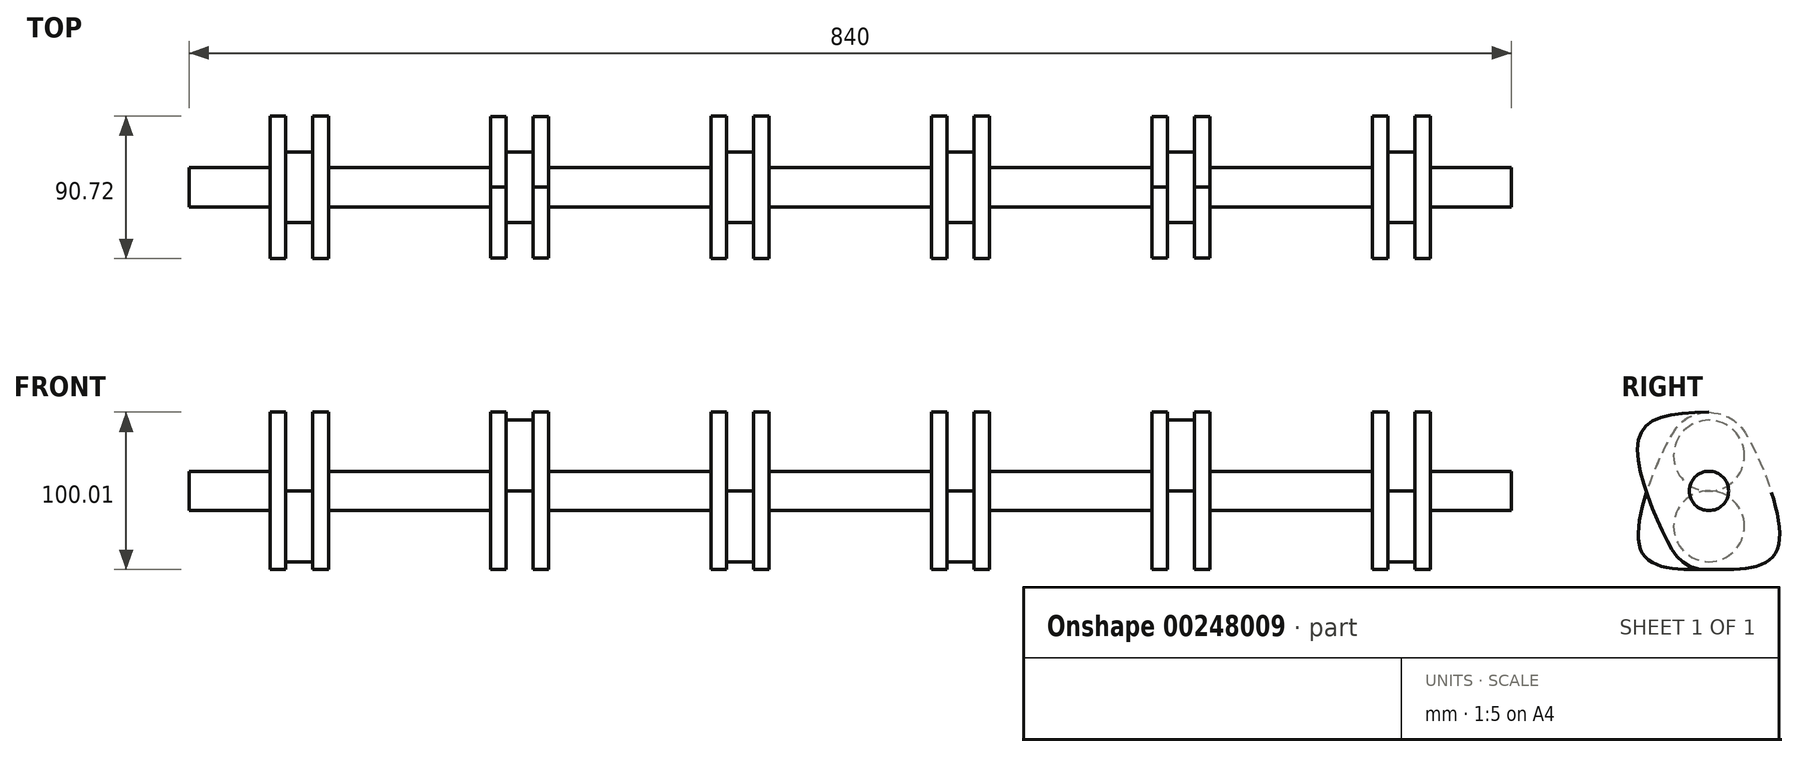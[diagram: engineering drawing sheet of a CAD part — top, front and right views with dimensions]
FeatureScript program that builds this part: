
annotation { "Feature Type Name" : "Feature", "Feature Type Description" : "" }
export const myFeature = defineFeature(function(context is Context, id is Id, definition is map)
    precondition{}
    {
        {
            var Q0;
            Q0=qCreatedBy(makeId("Front.planeOp"),FACE);
            var sketch = newSketch(context, id + "F0", { "sketchPlane" : qUnion([Q0])});
            skLineSegment(sketch, "E0", {"start": v(-435, 99.47) * mm, "end": v(-435, -63.15) * mm, "construction": true});
            skLineSegment(sketch, "E1", {"start": v(435, 93.37) * mm, "end": v(435, -121.08) * mm, "construction": true});
            skSolve(sketch);
        }
        {
            var Q0;
            Q0=qCreatedBy(makeId("Right.planeOp"),FACE);
            cPlane(context, id + "F1", {"entities" : qUnion([Q0]), "cplaneType" : CPlaneType.OFFSET, "offset" : 435 * mm, "width" : 150 * mm, "height" : 150 * mm});
        }
        {
            var Q0;
            Q0=qCreatedBy(id+"F1.planeOp",FACE);
            var sketch = newSketch(context, id + "F2", { "sketchPlane" : qUnion([Q0])});
            skCircle(sketch, "E2", {"center": v(0, 0) * mm, "radius": 12.5 * mm});
            skSolve(sketch);
        }
        {
            var Q0;
            Q0 = qSketchRegion(id + "F2", true);
            extrude(context, id + "F3", {"entities" : qUnion([Q0]), "oppositeDirection" : true, "depth" : 51.5 * mm});
        }
        {
            var Q0;
            Q0=makeQuery(id+"F3.opExtrude","CAP_FACE",FACE,{"disambiguationData":[OSD([sQuery(id+"F2.wireOp",EDGE,"E2")])],"isStart":false});
            var sketch = newSketch(context, id + "F4", { "sketchPlane" : qUnion([Q0])});
            skCircle(sketch, "E3", {"center": v(0, 0) * mm, "radius": 22.5 * mm, "construction": true});
            skLineSegment(sketch, "E4", {"start": v(-49.42, 50) * mm, "end": v(46.28, 50) * mm, "construction": true});
            skLineSegment(sketch, "E5", {"start": v(-54.63, -50) * mm, "end": v(61.91, -50) * mm, "construction": true});
            skFitSpline(sketch, "E6", {"points": [v(0, 50) * mm, v(-44.16, 34.7) * mm, v(-28.23, -28.04) * mm, v(0, -50) * mm], "startDerivative": vector(-213.04, 0) * mm, "endDerivative": vector(172.02, 0) * mm});
            skFitSpline(sketch, "E7.MirrorCS", {"points": [v(0, 50) * mm, v(44.16, 34.7) * mm, v(28.23, -28.04) * mm, v(0, -50) * mm], "startDerivative": vector(213.04, 0) * mm, "endDerivative": vector(-172.02, 0) * mm});
            skFitSpline(sketch, "E8.MirrorCS", {"points": [v(0, 50) * mm, v(44.16, 34.7) * mm, v(28.23, -28.04) * mm, v(0, -50) * mm], "startDerivative": vector(213.04, 0) * mm, "endDerivative": vector(-172.02, 0) * mm});
            skCircle(sketch, "E9", {"center": v(0, -22.5) * mm, "radius": 22.5 * mm, "construction": true});
            skSolve(sketch);
        }
        {
            var Q0;
            Q0 = qSketchRegion(id + "F4", true);
            extrude(context, id + "F5", {"entities" : qUnion([Q0]), "operationType" : NewBodyOperationType.ADD, "depth" : 10 * mm});
        }
        {
            var Q0;
            Q0=makeQuery(id+"F5.opExtrude","CAP_FACE",FACE,{"disambiguationData":[OSD([sQuery(id+"F4.wireOp",EDGE,"E6"),sQuery(id+"F4.wireOp",EDGE,"E8.MirrorCS")])],"isStart":false});
            var sketch = newSketch(context, id + "F6", { "sketchPlane" : qUnion([Q0])});
            skCircle(sketch, "E10", {"center": v(0, -22.45) * mm, "radius": 22.5 * mm});
            skSolve(sketch);
        }
        {
            var Q0;
            Q0 = qSketchRegion(id + "F6", true);
            extrude(context, id + "F7", {"entities" : qUnion([Q0]), "operationType" : NewBodyOperationType.ADD, "depth" : 8.5 * mm});
        }
        {
            var Q0;
            Q0=makeQuery(id+"F3.opExtrude","SWEPT_BODY",BODY,{"disambiguationData":[OSD([sQuery(id+"F2.wireOp",EDGE,"E2")])]});
            var Q1;
            Q1=makeQuery(id+"F7.opExtrude","CAP_FACE",FACE,{"disambiguationData":[OSD([sQuery(id+"F6.wireOp",EDGE,"E10")])],"isStart":false});
            mirror(context, id + "F8", {"operationType" : NewBodyOperationType.ADD, "entities" : qUnion([Q0]), "mirrorPlane" : qUnion([Q1])});
        }
        {
            var Q0;
            Q0=makeQuery(id+"F8.opPattern","COPY",FACE,{"derivedFrom":makeQuery(id+"F3.opExtrude","CAP_FACE",FACE,{"disambiguationData":[OSD([sQuery(id+"F2.wireOp",EDGE,"E2")])],"isStart":true}),"instanceName":"1"});
            var sketch = newSketch(context, id + "F9", { "sketchPlane" : qUnion([Q0])});
            skCircle(sketch, "E11", {"center": v(0, 0) * mm, "radius": 12.5 * mm});
            skSolve(sketch);
        }
        {
            var Q0;
            Q0=makeQuery(id+"F9.imprint","IMPRINT",FACE,{"disambiguationData":[TD([[makeQuery(id+"F9.imprint","IMPRINT",EDGE,{"derivedFrom":sQuery(id+"F9.wireOp",EDGE,"E11")}),-1.0]])]});
            var sketch = newSketch(context, id + "F10", { "sketchPlane" : qUnion([Q0])});
            skCircle(sketch, "E12", {"center": v(0, 0) * mm, "radius": 12.5 * mm});
            skSolve(sketch);
        }
        {
            var Q0;
            Q0 = qSketchRegion(id + "F10", true);
            extrude(context, id + "F11", {"entities" : qUnion([Q0]), "operationType" : NewBodyOperationType.ADD, "depth" : 51.5 * mm});
        }
        {
            var Q0;
            Q0=makeQuery(id+"F11.opExtrude","CAP_FACE",FACE,{"disambiguationData":[OSD([sQuery(id+"F10.wireOp",EDGE,"E12")])],"isStart":false});
            var sketch = newSketch(context, id + "F12", { "sketchPlane" : qUnion([Q0])});
            skLineSegment(sketch, "E13", {"start": v(0, 50) * mm, "end": v(55.91, 50) * mm, "construction": true});
            skLineSegment(sketch, "E14", {"start": v(0, -50) * mm, "end": v(45.26, -50) * mm, "construction": true});
            skCircle(sketch, "E15", {"center": v(0, 22.5) * mm, "radius": 22.5 * mm, "construction": true});
            skFitSpline(sketch, "E16", {"points": [v(0, 50) * mm, v(-16.75, 43.96) * mm, v(-27.38, 29.07) * mm, v(-43.06, -38.2) * mm, v(0, -50) * mm], "startDerivative": vector(-146.27, -12.32) * mm, "endDerivative": vector(191.84, 0.2) * mm});
            skLineSegment(sketch, "E17", {"start": v(-45.3, 25.93) * mm, "end": v(-45.3, -52.13) * mm, "construction": true});
            skFitSpline(sketch, "E18.MirrorCS", {"points": [v(0, 50) * mm, v(16.75, 43.96) * mm, v(27.38, 29.07) * mm, v(43.06, -38.2) * mm, v(0, -50) * mm], "startDerivative": vector(146.27, -12.32) * mm, "endDerivative": vector(-191.84, 0.2) * mm});
            skSolve(sketch);
        }
        {
            var Q0;
            Q0 = qSketchRegion(id + "F12", true);
            extrude(context, id + "F13", {"entities" : qUnion([Q0]), "operationType" : NewBodyOperationType.ADD, "depth" : 10 * mm});
        }
        {
            var Q0;
            Q0=makeQuery(id+"F13.opExtrude","CAP_FACE",FACE,{"disambiguationData":[OSD([sQuery(id+"F12.wireOp",EDGE,"E16"),sQuery(id+"F12.wireOp",EDGE,"E18.MirrorCS")])],"isStart":false});
            var sketch = newSketch(context, id + "F14", { "sketchPlane" : qUnion([Q0])});
            skCircle(sketch, "E19", {"center": v(0, 22.41) * mm, "radius": 22.5 * mm});
            skSolve(sketch);
        }
        {
            var Q0;
            Q0 = qSketchRegion(id + "F14", true);
            extrude(context, id + "F15", {"entities" : qUnion([Q0]), "operationType" : NewBodyOperationType.ADD, "depth" : 8.5 * mm});
        }
        {
            var Q0;
            Q0=makeQuery(id+"F3.opExtrude","SWEPT_BODY",BODY,{"disambiguationData":[OSD([sQuery(id+"F2.wireOp",EDGE,"E2")])]});
            var Q1;
            Q1=makeQuery(id+"F15.opExtrude","CAP_FACE",FACE,{"disambiguationData":[OSD([sQuery(id+"F14.wireOp",EDGE,"E19")])],"isStart":false});
            mirror(context, id + "F16", {"operationType" : NewBodyOperationType.ADD, "entities" : qUnion([Q0]), "mirrorPlane" : qUnion([Q1])});
        }
        {
            var Q0;
            Q0=makeQuery(id+"F3.opExtrude","SWEPT_BODY",BODY,{"disambiguationData":[OSD([sQuery(id+"F2.wireOp",EDGE,"E2")])]});
            var Q1;
            Q1=makeQuery(id+"F16.opPattern","COPY",FACE,{"derivedFrom":makeQuery(id+"F3.opExtrude","CAP_FACE",FACE,{"disambiguationData":[OSD([sQuery(id+"F2.wireOp",EDGE,"E2")])],"isStart":true}),"instanceName":"1"});
            mirror(context, id + "F17", {"operationType" : NewBodyOperationType.ADD, "entities" : qUnion([Q0]), "mirrorPlane" : qUnion([Q1])});
        }
    });
